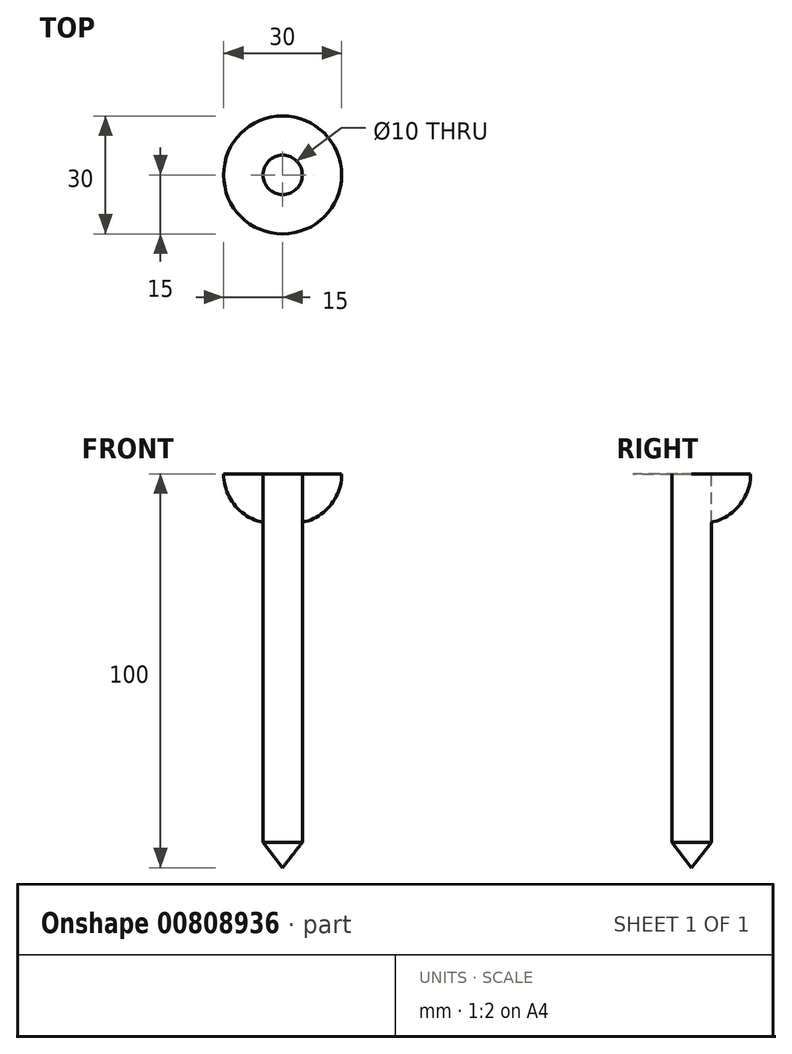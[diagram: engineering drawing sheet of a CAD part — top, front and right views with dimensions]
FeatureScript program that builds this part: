
annotation { "Feature Type Name" : "Feature", "Feature Type Description" : "" }
export const myFeature = defineFeature(function(context is Context, id is Id, definition is map)
    precondition{}
    {
        {
            var Q0;
            Q0=qCreatedBy(makeId("Front.planeOp"),FACE);
            var sketch = newSketch(context, id + "F0", { "sketchPlane" : qUnion([Q0])});
            skLineSegment(sketch, "E0", {"start": v(0, 0) * mm, "end": v(0, -100) * mm});
            skLineSegment(sketch, "E1", {"start": v(0, -100) * mm, "end": v(-5, -93.55) * mm});
            skLineSegment(sketch, "E2", {"start": v(-5, -93.55) * mm, "end": v(-5, 0) * mm});
            skLineSegment(sketch, "E3", {"start": v(-5, 0) * mm, "end": v(0, 0) * mm});
            skLineSegment(sketch, "E4", {"start": v(0, 0) * mm, "end": v(-15, 0) * mm});
            skArc(sketch, "E5", {"start": v(0, 12.25) * mm, "mid": v(-10.4, 9.68) * mm, "end": v(-15, 0) * mm});
            skLineSegment(sketch, "E6", {"start": v(0, 12.25) * mm, "end": v(0, 0) * mm});
            skSolve(sketch);
        }
        {
            var Q0;
            {var subQ3=sQuery(id+"F0.wireOp",EDGE,"E5");Q0=makeQuery(id+"F0.imprint","IMPRINT",FACE,{"disambiguationData":[TD([[makeQuery(id+"F0.imprint","IMPRINT",EDGE,{"derivedFrom":subQ3}),1.0]])]});}
            var Q1;
            {var subQ0=sQuery(id+"F0.wireOp",EDGE,"E0");Q1=makeQuery(id+"F0.imprint","IMPRINT",FACE,{"disambiguationData":[TD([[makeQuery(id+"F0.imprint","IMPRINT",EDGE,{"derivedFrom":subQ0}),-1.0]])]});}
            var Q2;
            Q2=sQuery(id+"F0.wireOp",EDGE,"E6");
            var Q3;
            Q3=sQuery(id+"F0.wireOp",EDGE,"E5");
            var Q4;
            Q4=sQuery(id+"F0.wireOp",EDGE,"E2");
            var Q5;
            Q5=sQuery(id+"F0.wireOp",EDGE,"E4");
            var Q6;
            Q6=sQuery(id+"F0.wireOp",EDGE,"E3");
            var Q7;
            Q7=sQuery(id+"F0.wireOp",EDGE,"E1");
            var Q8;
            Q8=sQuery(id+"F0.wireOp",EDGE,"E0");
            var Q9;
            Q9=sQuery(id+"F0.wireOp",EDGE,"E0");
            revolve(context, id + "F1", {"surfaceOperationType" : NewSurfaceOperationType.NEW, "entities" : qUnion([Q0, Q1]), "surfaceEntities" : qUnion([Q2, Q3, Q4, Q5, Q6, Q7, Q8]), "axis" : qUnion([Q9]), "revolveType" : RevolveType.FULL});
        }
    });
